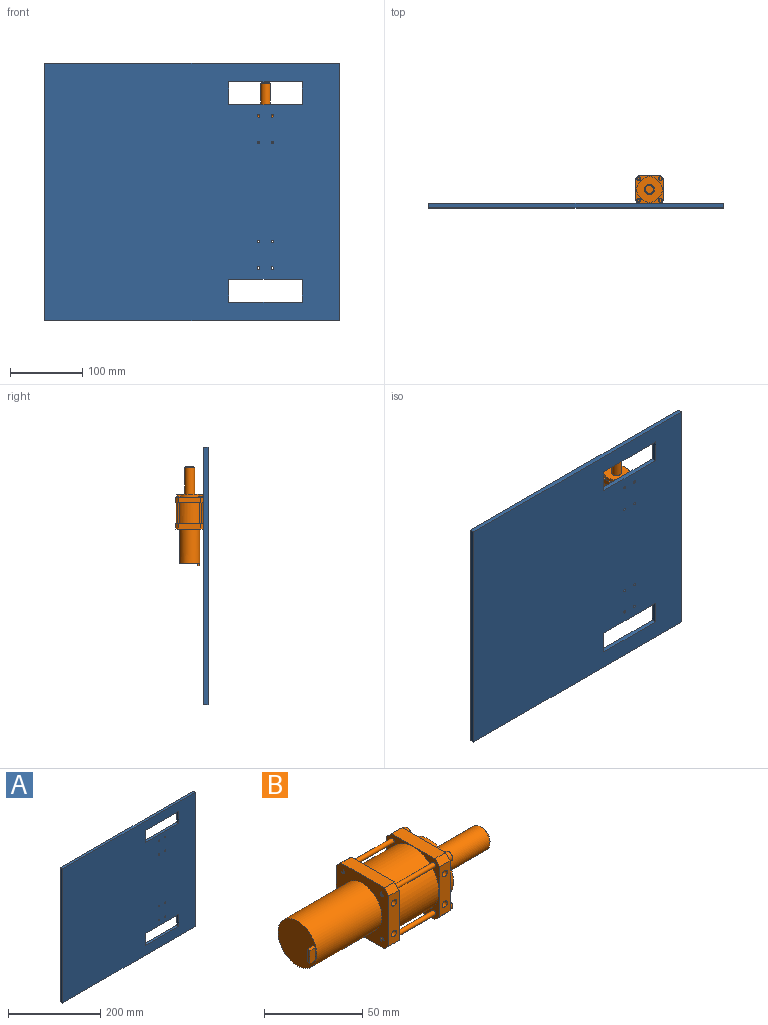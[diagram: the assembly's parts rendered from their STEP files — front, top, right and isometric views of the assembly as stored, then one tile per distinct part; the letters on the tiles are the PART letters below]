
ASSEMBLY  parts=2 mates=4
PART A: 22 faces, bbox 406.4x6.4x355.6 mm
  f0: cylinder r=1.84mm len=6.35mm, axis (0,1,0), area 73.5mm2, adj f19,f20
  f1: cylinder r=1.84mm len=6.35mm, axis (0,1,0), area 73.5mm2, adj f19,f20
  f2: cylinder r=1.84mm len=6.35mm, axis (0,1,0), area 73.5mm2, adj f19,f20
  f3: cylinder r=1.84mm len=6.35mm, axis (0,1,0), area 73.5mm2, adj f19,f20
  f4: cylinder r=1.84mm len=6.35mm, axis (0,1,0), area 73.5mm2, adj f19,f20
  f5: cylinder r=1.84mm len=6.35mm, axis (0,1,0), area 73.5mm2, adj f19,f20
  f6: cylinder r=1.84mm len=6.35mm, axis (0,1,0), area 73.5mm2, adj f19,f20
  f7: plane 31.75x6.35mm, normal (1,0,0), area 201.6mm2, adj f8,f10,f19,f20
  f8: plane 101.6x6.35mm, normal (0,0,-1), area 645.2mm2, adj f7,f9,f19,f20
  f9: plane 31.75x6.35mm, normal (-1,0,0), area 201.6mm2, adj f8,f10,f19,f20
  f10: plane 101.6x6.35mm, normal (0,0,1), area 645.2mm2, adj f7,f9,f19,f20
  f11: plane 31.75x6.35mm, normal (-1,0,0), area 201.6mm2, adj f12,f14,f19,f20
  f12: plane 101.6x6.35mm, normal (0,0,1), area 645.2mm2, adj f11,f13,f19,f20
  f13: plane 31.75x6.35mm, normal (1,0,0), area 201.6mm2, adj f12,f14,f19,f20
  f14: plane 101.6x6.35mm, normal (0,0,-1), area 645.2mm2, adj f11,f13,f19,f20
  f15: plane 406.4x6.35mm, normal (0,0,1), area 2580.6mm2, adj f16,f18,f19,f20
  f16: plane 355.6x6.35mm, normal (-1,0,0), area 2258.1mm2, adj f15,f17,f19,f20
  f17: plane 406.4x6.35mm, normal (0,0,-1), area 2580.6mm2, adj f16,f18,f19,f20
  f18: plane 355.6x6.35mm, normal (1,0,0), area 2258.1mm2, adj f15,f17,f19,f20
  f19: plane 406.4x355.6mm, normal (0,1,0), area 137979mm2, adj f0,f1,f2,f3,f4,f5,f6,f7
  f20: plane 406.4x355.6mm, normal (0,-1,0), area 137979mm2, adj f0,f1,f2,f3,f4,f5,f6,f7
  f21: cylinder r=1.84mm len=6.35mm, axis (0,1,0), area 73.5mm2, adj f19,f20
PART B: 96 faces, bbox 137.2x38x38 mm
  f0: plane 8x2mm, normal (-1,0,0), area 16mm2, adj f1,f2,f3,f4
  f1: plane 8x4mm, normal (0,1,0), area 32mm2, adj f0,f2,f4,f15
  f2: plane 4x2mm, normal (0,0,-1), area 8mm2, adj f0,f1,f3,f15
  f3: plane 8x4mm, normal (0,-1,0), area 32mm2, adj f0,f2,f4,f15
  f4: plane 4x2mm, normal (0,0,1), area 8mm2, adj f0,f1,f3,f15
  f5: cone r=0.92mm half-angle=59deg, axis (0,1,0), area 12.4mm2, adj f16
  f6: cone r=0.92mm half-angle=59deg, axis (0,1,0), area 12.4mm2, adj f17
  f7: cone r=0.92mm half-angle=59deg, axis (0,-1,0), area 12.4mm2, adj f18
  f8: cone r=0.92mm half-angle=59deg, axis (0,-1,0), area 12.4mm2, adj f19
  f9: plane 3.53x3.06mm, normal (1,0,0), area 8.1mm2, adj f20,f21,f22,f23,f24,f25
  f10: plane 3.53x3.06mm, normal (1,0,0), area 8.1mm2, adj f26,f27,f28,f29,f30,f31
  f11: plane 3.53x3.06mm, normal (1,0,0), area 8.1mm2, adj f32,f33,f34,f35,f36,f37
  f12: plane 3.53x3.06mm, normal (1,0,0), area 8.1mm2, adj f38,f39,f40,f41,f42,f43
  f13: cone r=6.29mm half-angle=45deg, axis (-1,0,0), area 56.7mm2, adj f14,f45,f46,f47
  f14: plane 11.65x11.36mm, normal (1,0,0), area 100.8mm2, adj f13,f44,f45,f47
  f15: plane 28.52x28mm, normal (-1,0,0), area 599.8mm2, adj f1,f2,f3,f4,f50
  f16: cylinder r=1.84mm len=12.7mm, axis (0,-1,0), area 146.9mm2, adj f5,f53
  f17: cylinder r=1.84mm len=12.7mm, axis (0,-1,0), area 146.9mm2, adj f6,f53
  f18: cylinder r=1.84mm len=12.7mm, axis (0,1,0), area 146.9mm2, adj f7,f57
  f19: cylinder r=1.84mm len=12.7mm, axis (0,1,0), area 146.9mm2, adj f8,f57
  f20: plane 1.86x1.53mm, normal (0,-0.5,-0.87), area 3.3mm2, adj f9,f21,f25,f59
  f21: plane 1.86x1.77mm, normal (0,-1,0), area 3.3mm2, adj f9,f20,f22,f59
  f22: plane 1.86x1.53mm, normal (0,-0.5,0.87), area 3.3mm2, adj f9,f21,f23,f59
  f23: plane 1.86x1.53mm, normal (0,0.5,0.87), area 3.3mm2, adj f9,f22,f24,f59
  f24: plane 1.86x1.77mm, normal (0,1,0), area 3.3mm2, adj f9,f23,f25,f59
  f25: plane 1.86x1.53mm, normal (0,0.5,-0.87), area 3.3mm2, adj f9,f20,f24,f59
  f26: plane 1.86x1.53mm, normal (0,-0.5,-0.87), area 3.3mm2, adj f10,f27,f31,f60
  f27: plane 1.86x1.77mm, normal (0,-1,0), area 3.3mm2, adj f10,f26,f28,f60
  f28: plane 1.86x1.53mm, normal (0,-0.5,0.87), area 3.3mm2, adj f10,f27,f29,f60
  f29: plane 1.86x1.53mm, normal (0,0.5,0.87), area 3.3mm2, adj f10,f28,f30,f60
  f30: plane 1.86x1.77mm, normal (0,1,0), area 3.3mm2, adj f10,f29,f31,f60
  f31: plane 1.86x1.53mm, normal (0,0.5,-0.87), area 3.3mm2, adj f10,f26,f30,f60
  f32: plane 1.86x1.53mm, normal (0,-0.5,-0.87), area 3.3mm2, adj f11,f33,f37,f61
  f33: plane 1.86x1.77mm, normal (0,-1,0), area 3.3mm2, adj f11,f32,f34,f61
  f34: plane 1.86x1.53mm, normal (0,-0.5,0.87), area 3.3mm2, adj f11,f33,f35,f61
  f35: plane 1.86x1.53mm, normal (0,0.5,0.87), area 3.3mm2, adj f11,f34,f36,f61
  f36: plane 1.86x1.77mm, normal (0,1,0), area 3.3mm2, adj f11,f35,f37,f61
  f37: plane 1.86x1.53mm, normal (0,0.5,-0.87), area 3.3mm2, adj f11,f32,f36,f61
  f38: plane 1.86x1.53mm, normal (0,-0.5,-0.87), area 3.3mm2, adj f12,f39,f43,f62
  f39: plane 1.86x1.77mm, normal (0,-1,0), area 3.3mm2, adj f12,f38,f40,f62
  f40: plane 1.86x1.53mm, normal (0,-0.5,0.87), area 3.3mm2, adj f12,f39,f41,f62
  f41: plane 1.86x1.53mm, normal (0,0.5,0.87), area 3.3mm2, adj f12,f40,f42,f62
  f42: plane 1.86x1.77mm, normal (0,1,0), area 3.3mm2, adj f12,f41,f43,f62
  f43: plane 1.86x1.53mm, normal (0,0.5,-0.87), area 3.3mm2, adj f12,f38,f42,f62
  f44: plane 38.11x3mm, normal (0,0,-1), area 114.3mm2, adj f14,f45,f47,f63
  f45: plane 38.16x1.89mm, normal (0,1,0), area 69.6mm2, adj f13,f14,f44,f46,f63
  f46: cylinder r=6.83mm len=37.01mm, axis (1,0,0), area 1477.5mm2, adj f13,f45,f47,f63
  f47: plane 38.16x1.89mm, normal (0,-1,0), area 69.6mm2, adj f13,f14,f44,f46,f63
  f48: cone r=0.92mm half-angle=59deg, axis (0,1,0), area 12.4mm2, adj f66
  f49: cone r=0.92mm half-angle=59deg, axis (0,1,0), area 12.4mm2, adj f67
  f50: cylinder r=14mm len=47mm, axis (-1,0,0), area 4134.3mm2, adj f15,f71
  f51: plane 31.18x7.37mm, normal (0,0,-1), area 229.8mm2, adj f52,f58,f69,f71
  f52: plane 7.37x3.41mm, normal (0,0.71,-0.71), area 35.5mm2, adj f51,f53,f69,f71
  f53: plane 31.18x7.37mm, normal (0,1,0), area 208.5mm2, adj f16,f17,f52,f54,f69,f71
  f54: plane 7.37x3.41mm, normal (0,0.71,0.71), area 35.5mm2, adj f53,f55,f69,f71
  f55: plane 31.18x7.37mm, normal (0,0,1), area 229.8mm2, adj f54,f56,f69,f71
  f56: plane 7.37x3.41mm, normal (0,-0.71,0.71), area 35.5mm2, adj f55,f57,f69,f71
  f57: plane 31.18x7.37mm, normal (0,-1,0), area 208.5mm2, adj f18,f19,f56,f58,f69,f71
  f58: plane 7.37x3.41mm, normal (0,-0.71,-0.71), area 35.5mm2, adj f51,f57,f69,f71
  f59: plane 5.65x5.55mm, normal (1,0,0), area 16.1mm2, adj f20,f21,f22,f23,f24,f25,f73
  f60: plane 5.65x5.55mm, normal (1,0,0), area 16.1mm2, adj f26,f27,f28,f29,f30,f31,f74
  f61: plane 5.65x5.55mm, normal (1,0,0), area 16.1mm2, adj f32,f33,f34,f35,f36,f37,f75
  f62: plane 5.65x5.55mm, normal (1,0,0), area 16.1mm2, adj f38,f39,f40,f41,f42,f43,f76
  f63: plane 35.65x35mm, normal (1,0,0), area 821.2mm2, adj f44,f45,f46,f47,f77
  f64: cylinder r=1.32mm len=7.37mm, axis (1,0,0), area 38.9mm2, adj f69,f71,f78
  f65: cylinder r=1.32mm len=7.37mm, axis (1,0,0), area 38.4mm2, adj f69,f71,f79
  f66: cylinder r=1.84mm len=12.7mm, axis (0,-1,0), area 146.9mm2, adj f48,f82
  f67: cylinder r=1.84mm len=12.7mm, axis (0,-1,0), area 146.9mm2, adj f49,f82
  f68: cylinder r=1.32mm len=7.37mm, axis (1,0,0), area 37.8mm2, adj f69,f71,f86
  f69: plane 38x38mm, normal (1,0,0), area 313mm2, adj f51,f52,f53,f54,f55,f56,f57,f58
  f70: cylinder r=1.32mm len=7.37mm, axis (1,0,0), area 38.4mm2, adj f69,f71,f87
  f71: plane 38x38mm, normal (-1,0,0), area 794.4mm2, adj f50,f51,f52,f53,f54,f55,f56,f57
  f72: cone r=0.92mm half-angle=59deg, axis (0,-1,0), area 12.4mm2, adj f88
  f73: cylinder r=2.77mm len=5.55mm, axis (1,0,0), area 54.9mm2, adj f59,f90
  f74: cylinder r=2.77mm len=5.55mm, axis (1,0,0), area 54.9mm2, adj f60,f90
  f75: cylinder r=2.77mm len=5.55mm, axis (1,0,0), area 54.9mm2, adj f61,f90
  f76: cylinder r=2.77mm len=5.55mm, axis (1,0,0), area 54.9mm2, adj f62,f90
  f77: cylinder r=17.5mm len=35mm, axis (1,0,0), area 439.8mm2, adj f63,f90
  f78: cylinder r=1.32mm len=36.54mm, axis (-1,0,0), area 264.4mm2, adj f64,f69,f71,f92
  f79: cylinder r=1.32mm len=36.54mm, axis (-1,0,0), area 264.9mm2, adj f65,f69,f71,f92
  f80: plane 31.18x7.53mm, normal (0,0,-1), area 234.8mm2, adj f81,f89,f90,f92
  f81: plane 7.53x3.41mm, normal (0,0.71,-0.71), area 36.3mm2, adj f80,f82,f90,f92
  f82: plane 31.18x7.53mm, normal (0,1,0), area 213.5mm2, adj f66,f67,f81,f83,f90,f92
  f83: plane 7.53x3.41mm, normal (0,0.71,0.71), area 36.3mm2, adj f82,f84,f90,f92
  f84: plane 31.18x7.53mm, normal (0,0,1), area 234.8mm2, adj f83,f90,f91,f92
  f85: cylinder r=18.5mm len=37mm, axis (1,0,0), area 3390.7mm2, adj f69,f92
  f86: cylinder r=1.32mm len=36.54mm, axis (-1,0,0), area 265.5mm2, adj f68,f69,f71,f92
  f87: cylinder r=1.32mm len=36.54mm, axis (-1,0,0), area 264.9mm2, adj f69,f70,f71,f92
  f88: cylinder r=1.84mm len=12.7mm, axis (0,1,0), area 146.9mm2, adj f72,f93
  f89: plane 7.53x3.41mm, normal (0,-0.71,-0.71), area 36.3mm2, adj f80,f90,f92,f93
  f90: plane 38x38mm, normal (1,0,0), area 361.9mm2, adj f73,f74,f75,f76,f77,f80,f81,f82
  f91: plane 7.53x3.41mm, normal (0,-0.71,0.71), area 36.3mm2, adj f84,f90,f92,f93
  f92: plane 38x38mm, normal (-1,0,0), area 323.6mm2, adj f78,f79,f80,f81,f82,f83,f84,f85
  f93: plane 31.18x7.53mm, normal (0,-1,0), area 213.5mm2, adj f88,f89,f90,f91,f92,f94
  f94: cylinder r=1.84mm len=12.7mm, axis (0,1,0), area 146.9mm2, adj f93,f95
  f95: cone r=0.92mm half-angle=59deg, axis (0,-1,0), area 12.4mm2, adj f94
PLACE A t=(-5.67,-3.02,-6.9)mm fixed
PLACE B rot(axis=(0,-1,0),90deg) t=(95.93,19.15,57.99)mm
MATE cylindrical B.f6 <-> A.f4  axis (0,1,0) through (105.46,0.15,61.68)mm
MATE planar B.f93 <-> A.f19  axis (0,-1,0) through (95.93,0.15,98.3)mm
MATE parallel B.f53 <-> A.f19  axis (0,1,0) through (95.93,38.15,61.68)mm
MATE parallel B.f63 <-> A.f15  axis (0,0,1) through (95.97,19.15,106.06)mm
